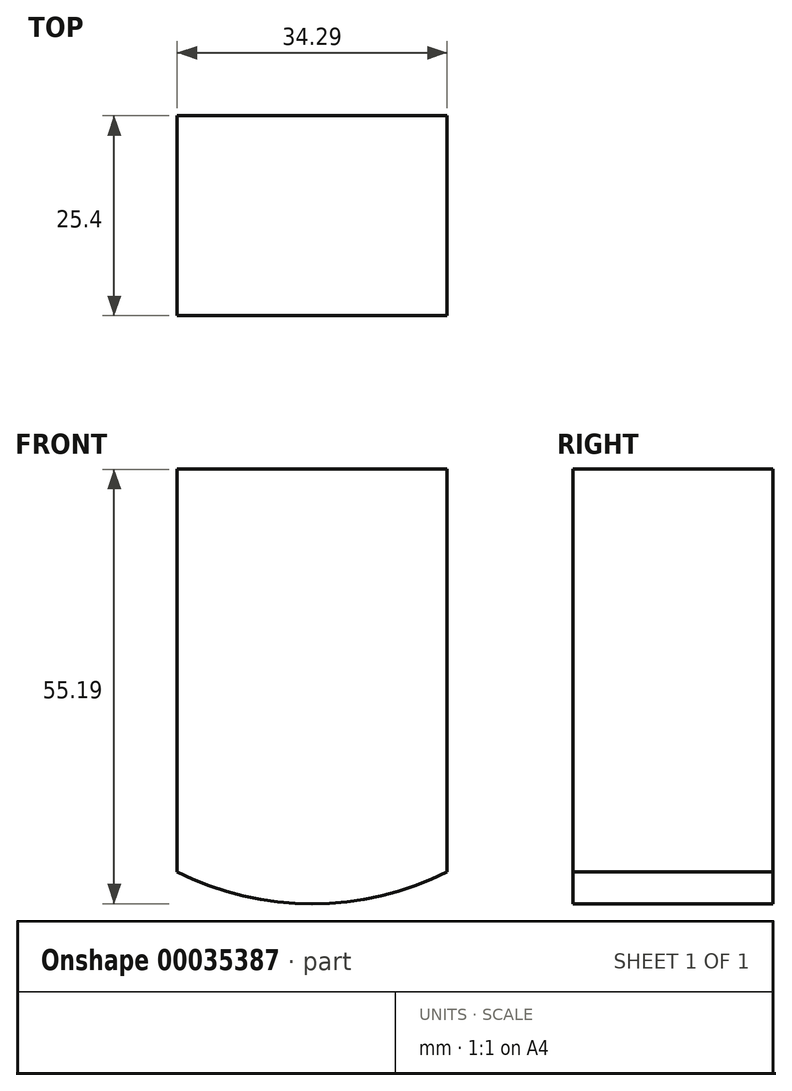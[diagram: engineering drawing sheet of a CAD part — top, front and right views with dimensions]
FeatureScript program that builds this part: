
annotation { "Feature Type Name" : "Feature", "Feature Type Description" : "" }
export const myFeature = defineFeature(function(context is Context, id is Id, definition is map)
    precondition{}
    {
        {
            var Q0;
            Q0=qCreatedBy(makeId("Front.planeOp"),FACE);
            var sketch = newSketch(context, id + "F0", { "sketchPlane" : qUnion([Q0])});
            skLineSegment(sketch, "E0", {"start": v(-23.29, 56.86) * mm, "end": v(-23.29, 5.72) * mm});
            skLineSegment(sketch, "E1", {"start": v(11, 56.86) * mm, "end": v(11, 5.72) * mm});
            skArc(sketch, "E2", {"start": v(-23.29, 5.72) * mm, "mid": v(-6.14, 1.67) * mm, "end": v(11, 5.72) * mm});
            skLineSegment(sketch, "E3", {"start": v(-23.29, 56.86) * mm, "end": v(11, 56.86) * mm});
            skSolve(sketch);
        }
        {
            var Q0;
            Q0 = qSketchRegion(id + "F0", true);
            extrude(context, id + "F1", {"entities" : qUnion([Q0]), "depth" : 25.4 * mm});
        }
    });
